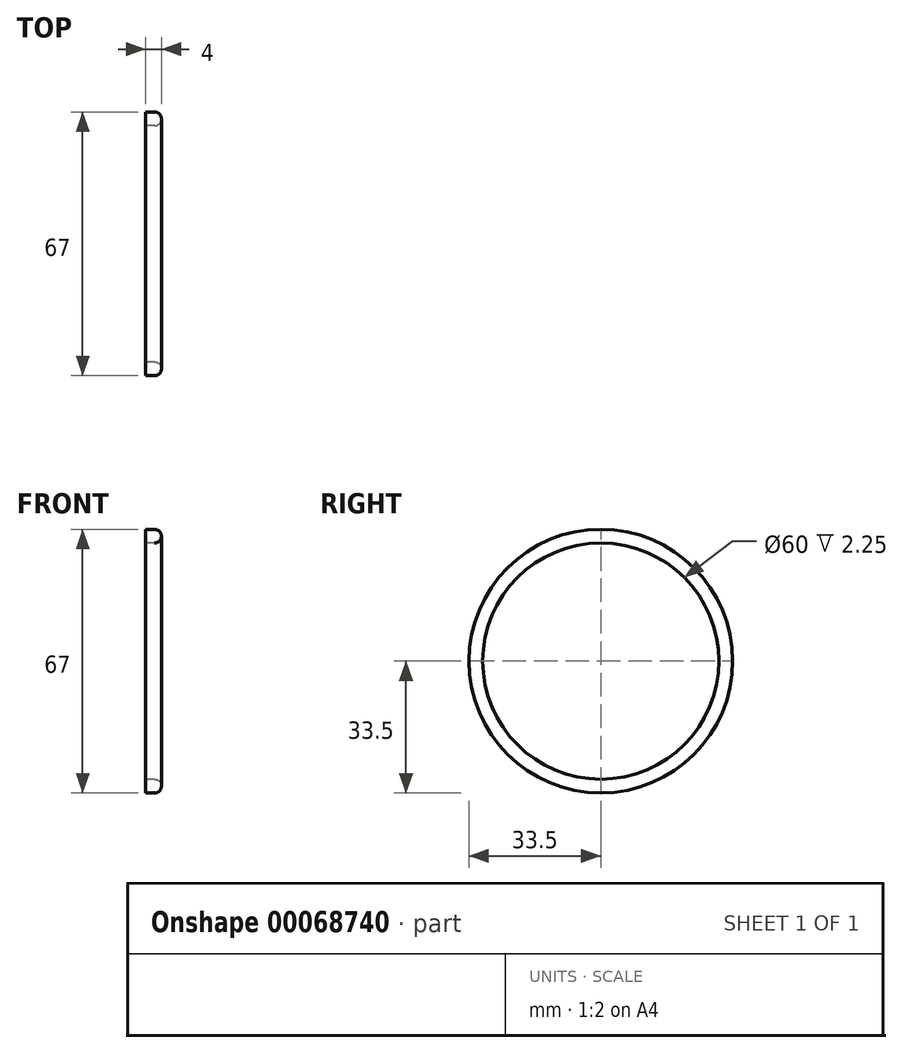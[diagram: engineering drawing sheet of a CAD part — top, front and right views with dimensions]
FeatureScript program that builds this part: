
annotation { "Feature Type Name" : "Feature", "Feature Type Description" : "" }
export const myFeature = defineFeature(function(context is Context, id is Id, definition is map)
    precondition{}
    {
        {
            var Q0;
            Q0=qCreatedBy(makeId("Top.planeOp"),FACE);
            var sketch = newSketch(context, id + "F0", { "sketchPlane" : qUnion([Q0])});
            skLineSegment(sketch, "E0.bottom", {"start": v(0, 33.5) * mm, "end": v(2.25, 33.5) * mm});
            skLineSegment(sketch, "E0.top", {"start": v(0, 30) * mm, "end": v(2.25, 30) * mm});
            skLineSegment(sketch, "E0.left", {"start": v(0, 33.5) * mm, "end": v(0, 30) * mm});
            skLineSegment(sketch, "E0.right", {"start": v(2.25, 33.5) * mm, "end": v(2.25, 30) * mm});
            skArc(sketch, "E1", {"start": v(2.25, 30) * mm, "mid": v(4, 31.75) * mm, "end": v(2.25, 33.5) * mm});
            skLineSegment(sketch, "E2", {"start": v(-71.2, 0) * mm, "end": v(72.04, 0) * mm, "construction": true});
            skSolve(sketch);
        }
        {
            var Q0;
            Q0 = qSketchRegion(id + "F0", true);
            var Q1;
            Q1=sQuery(id+"F0.wireOp",EDGE,"E2");
            revolve(context, id + "F1", {"entities" : qUnion([Q0]), "axis" : qUnion([Q1]), "revolveType" : RevolveType.FULL});
        }
    });
